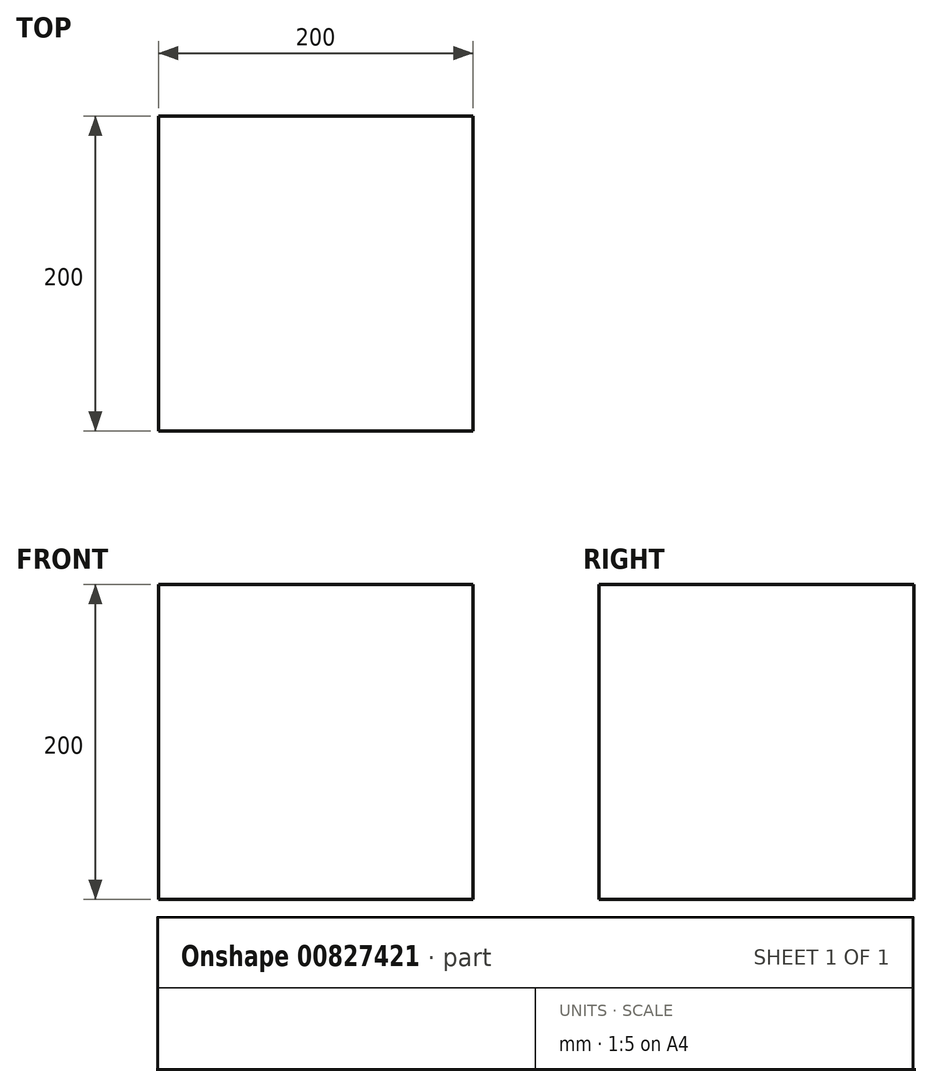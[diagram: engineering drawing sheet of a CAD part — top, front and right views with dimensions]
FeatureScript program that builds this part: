
annotation { "Feature Type Name" : "Feature", "Feature Type Description" : "" }
export const myFeature = defineFeature(function(context is Context, id is Id, definition is map)
    precondition{}
    {
        {
            var Q0;
            Q0=qCreatedBy(makeId("Front.planeOp"),FACE);
            var sketch = newSketch(context, id + "F0", { "sketchPlane" : qUnion([Q0])});
            skLineSegment(sketch, "E0.bottom", {"start": v(0, 0) * mm, "end": v(200, 0) * mm});
            skLineSegment(sketch, "E0.top", {"start": v(0, 200) * mm, "end": v(200, 200) * mm});
            skLineSegment(sketch, "E0.left", {"start": v(0, 0) * mm, "end": v(0, 200) * mm});
            skLineSegment(sketch, "E0.right", {"start": v(200, 0) * mm, "end": v(200, 200) * mm});
            skSolve(sketch);
        }
        {
            var Q0;
            Q0=makeQuery(id+"F0.imprint","IMPRINT",FACE,{"disambiguationData":[TD([[makeQuery(id+"F0.imprint","IMPRINT",EDGE,{"derivedFrom":sQuery(id+"F0.wireOp",EDGE,"E0.bottom")}),1.0]])]});
            extrude(context, id + "F1", {"entities" : qUnion([Q0]), "depth" : 200 * mm, "offsetDistance" : 25 * mm});
        }
    });
